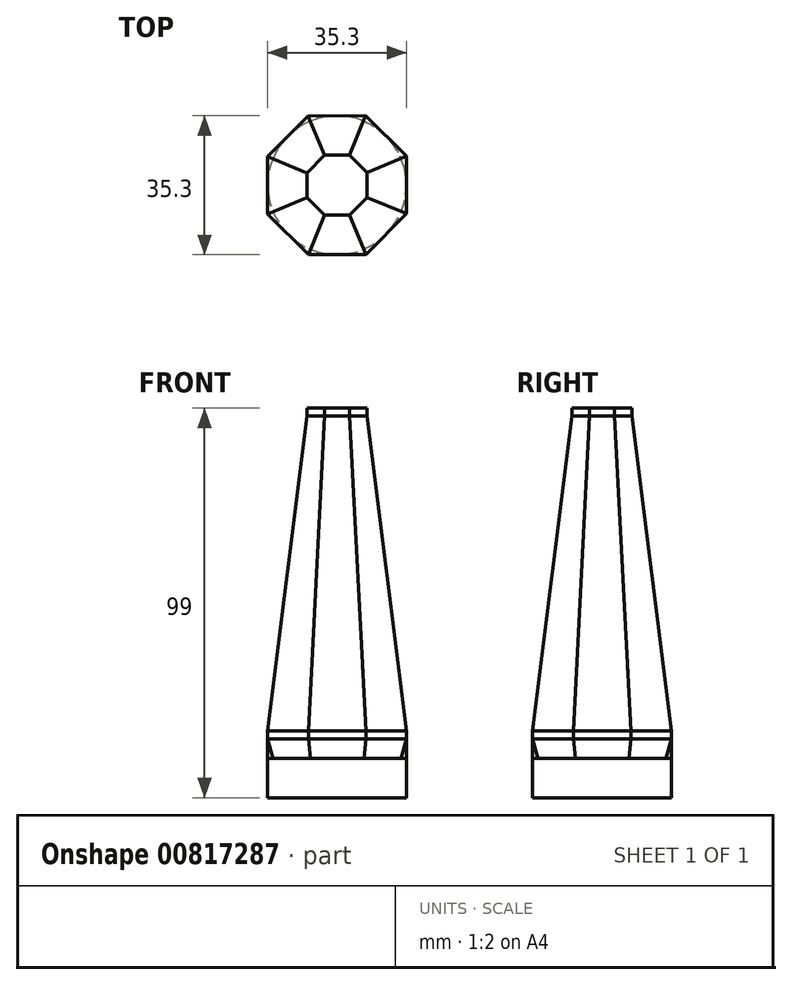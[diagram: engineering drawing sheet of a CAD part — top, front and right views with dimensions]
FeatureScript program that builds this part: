
annotation { "Feature Type Name" : "Feature", "Feature Type Description" : "" }
export const myFeature = defineFeature(function(context is Context, id is Id, definition is map)
    precondition{}
    {
        {
            var Q0;
            Q0=qCreatedBy(makeId("Top.planeOp"),FACE);
            var sketch = newSketch(context, id + "F0", { "sketchPlane" : qUnion([Q0])});
            skCircle(sketch, "E0", {"center": v(0, 0) * mm, "radius": 17.62 * mm});
            skSolve(sketch);
        }
        {
            var Q0;
            Q0 = qSketchRegion(id + "F0", true);
            var Q1;
            Q1 = qSketchRegion(id + "F2", true);
            extrude(context, id + "F1", {"entities" : qUnion([Q0, Q1]), "depth" : 10 * mm, "offsetDistance" : 25 * mm});
        }
        {
            var Q0;
            Q0=makeQuery(id+"F1.opExtrude","CAP_FACE",FACE,{"disambiguationData":[OSD([sQuery(id+"F0.wireOp",EDGE,"E0")])],"isStart":false});
            var sketch = newSketch(context, id + "F2", { "sketchPlane" : qUnion([Q0])});
            skCircle(sketch, "E1.cCircle", {"center": v(0, 0) * mm, "radius": 17.62 * mm, "construction": true});
            skLineSegment(sketch, "E1.0", {"start": v(17.65, -7.24) * mm, "end": v(7.36, -17.6) * mm});
            skLineSegment(sketch, "E1.1", {"start": v(7.36, -17.6) * mm, "end": v(-7.24, -17.65) * mm});
            skLineSegment(sketch, "E1.2", {"start": v(-7.24, -17.65) * mm, "end": v(-17.6, -7.36) * mm});
            skLineSegment(sketch, "E1.3", {"start": v(-17.6, -7.36) * mm, "end": v(-17.65, 7.24) * mm});
            skLineSegment(sketch, "E1.4", {"start": v(-17.65, 7.24) * mm, "end": v(-7.36, 17.6) * mm});
            skLineSegment(sketch, "E1.5", {"start": v(-7.36, 17.6) * mm, "end": v(7.24, 17.65) * mm});
            skLineSegment(sketch, "E1.6", {"start": v(7.24, 17.65) * mm, "end": v(17.6, 7.36) * mm});
            skLineSegment(sketch, "E1.7", {"start": v(17.6, 7.36) * mm, "end": v(17.65, -7.24) * mm});
            skPoint(sketch, "E1.0.midPoint", {"position": v(12.5, -12.42) * mm});
            skSolve(sketch);
        }
        {
            var Q0;
            Q0 = qSketchRegion(id + "F2", true);
            extrude(context, id + "F3", {"entities" : qUnion([Q0]), "depth" : 7 * mm, "offsetDistance" : 25 * mm, "hasSecondDirection" : true, "secondDirectionOppositeDirection" : true, "secondDirectionDepth" : -5 * mm});
        }
        {
            var Q0;
            Q0=makeQuery(id+"F3.opExtrude","CAP_FACE",FACE,{"disambiguationData":[OSD([sQuery(id+"F2.wireOp",EDGE,"E1.0"),sQuery(id+"F2.wireOp",EDGE,"E1.1"),sQuery(id+"F2.wireOp",EDGE,"E1.2"),sQuery(id+"F2.wireOp",EDGE,"E1.3"),sQuery(id+"F2.wireOp",EDGE,"E1.4"),sQuery(id+"F2.wireOp",EDGE,"E1.5"),sQuery(id+"F2.wireOp",EDGE,"E1.6"),sQuery(id+"F2.wireOp",EDGE,"E1.7")])],"isStart":false});
            cPlane(context, id + "F4", {"entities" : qUnion([Q0]), "cplaneType" : CPlaneType.OFFSET, "offset" : 80 * mm, "width" : 150 * mm, "height" : 150 * mm});
        }
        {
            var Q0;
            Q0=qCreatedBy(id+"F4.planeOp",FACE);
            var sketch = newSketch(context, id + "F5", { "sketchPlane" : qUnion([Q0])});
            skLineSegment(sketch, "E2.0", {"start": v(-7.61, -3.18) * mm, "end": v(-7.64, 3.13) * mm});
            skLineSegment(sketch, "E2.1", {"start": v(-3.13, -7.64) * mm, "end": v(-7.61, -3.18) * mm});
            skLineSegment(sketch, "E2.2", {"start": v(-7.64, 3.13) * mm, "end": v(-3.18, 7.61) * mm});
            skLineSegment(sketch, "E2.3", {"start": v(3.18, -7.61) * mm, "end": v(-3.13, -7.64) * mm});
            skLineSegment(sketch, "E2.4", {"start": v(-3.18, 7.61) * mm, "end": v(3.13, 7.64) * mm});
            skLineSegment(sketch, "E2.5", {"start": v(3.13, 7.64) * mm, "end": v(7.61, 3.18) * mm});
            skLineSegment(sketch, "E2.6", {"start": v(7.61, 3.18) * mm, "end": v(7.64, -3.13) * mm});
            skLineSegment(sketch, "E2.7", {"start": v(7.64, -3.13) * mm, "end": v(3.18, -7.61) * mm});
            skSolve(sketch);
        }
        {
            var Q0;
            Q0 = qSketchRegion(id + "F5", true);
            extrude(context, id + "F6", {"entities" : qUnion([Q0]), "depth" : 2 * mm, "offsetDistance" : 25 * mm});
        }
        {
            var Q0;
            Q0=makeQuery(id+"F3.opExtrude","CAP_FACE",FACE,{"disambiguationData":[OSD([sQuery(id+"F2.wireOp",EDGE,"E1.0"),sQuery(id+"F2.wireOp",EDGE,"E1.1"),sQuery(id+"F2.wireOp",EDGE,"E1.2"),sQuery(id+"F2.wireOp",EDGE,"E1.3"),sQuery(id+"F2.wireOp",EDGE,"E1.4"),sQuery(id+"F2.wireOp",EDGE,"E1.5"),sQuery(id+"F2.wireOp",EDGE,"E1.6"),sQuery(id+"F2.wireOp",EDGE,"E1.7")])],"isStart":false});
            var Q1;
            Q1=makeQuery(id+"F6.opExtrude","CAP_FACE",FACE,{"disambiguationData":[OSD([sQuery(id+"F5.wireOp",EDGE,"E2.0"),sQuery(id+"F5.wireOp",EDGE,"E2.1"),sQuery(id+"F5.wireOp",EDGE,"E2.2"),sQuery(id+"F5.wireOp",EDGE,"E2.3"),sQuery(id+"F5.wireOp",EDGE,"E2.4"),sQuery(id+"F5.wireOp",EDGE,"E2.5"),sQuery(id+"F5.wireOp",EDGE,"E2.6"),sQuery(id+"F5.wireOp",EDGE,"E2.7")])],"isStart":true});
            loft(context, id + "F7", {"operationType" : NewBodyOperationType.ADD, "sheetProfilesArray" : [{ "sheetProfileEntities" : qUnion([Q0]) }, { "sheetProfileEntities" : qUnion([Q1]) }]});
        }
        {
            var Q1;
            Q1=makeQuery(id+"F3.opExtrude","CAP_FACE",FACE,{"disambiguationData":[OSD([sQuery(id+"F2.wireOp",EDGE,"E1.0"),sQuery(id+"F2.wireOp",EDGE,"E1.1"),sQuery(id+"F2.wireOp",EDGE,"E1.2"),sQuery(id+"F2.wireOp",EDGE,"E1.3"),sQuery(id+"F2.wireOp",EDGE,"E1.4"),sQuery(id+"F2.wireOp",EDGE,"E1.5"),sQuery(id+"F2.wireOp",EDGE,"E1.6"),sQuery(id+"F2.wireOp",EDGE,"E1.7")])],"isStart":true});
            var Q2;
            Q2=makeQuery(id+"F1.opExtrude","CAP_FACE",FACE,{"disambiguationData":[OSD([sQuery(id+"F0.wireOp",EDGE,"E0")])],"isStart":false});
            loft(context, id + "F8", {"operationType" : NewBodyOperationType.ADD, "sheetProfilesArray" : [{ "sheetProfileEntities" : qUnion([Q1]) }, { "sheetProfileEntities" : qUnion([Q2]) }]});
        }
    });
